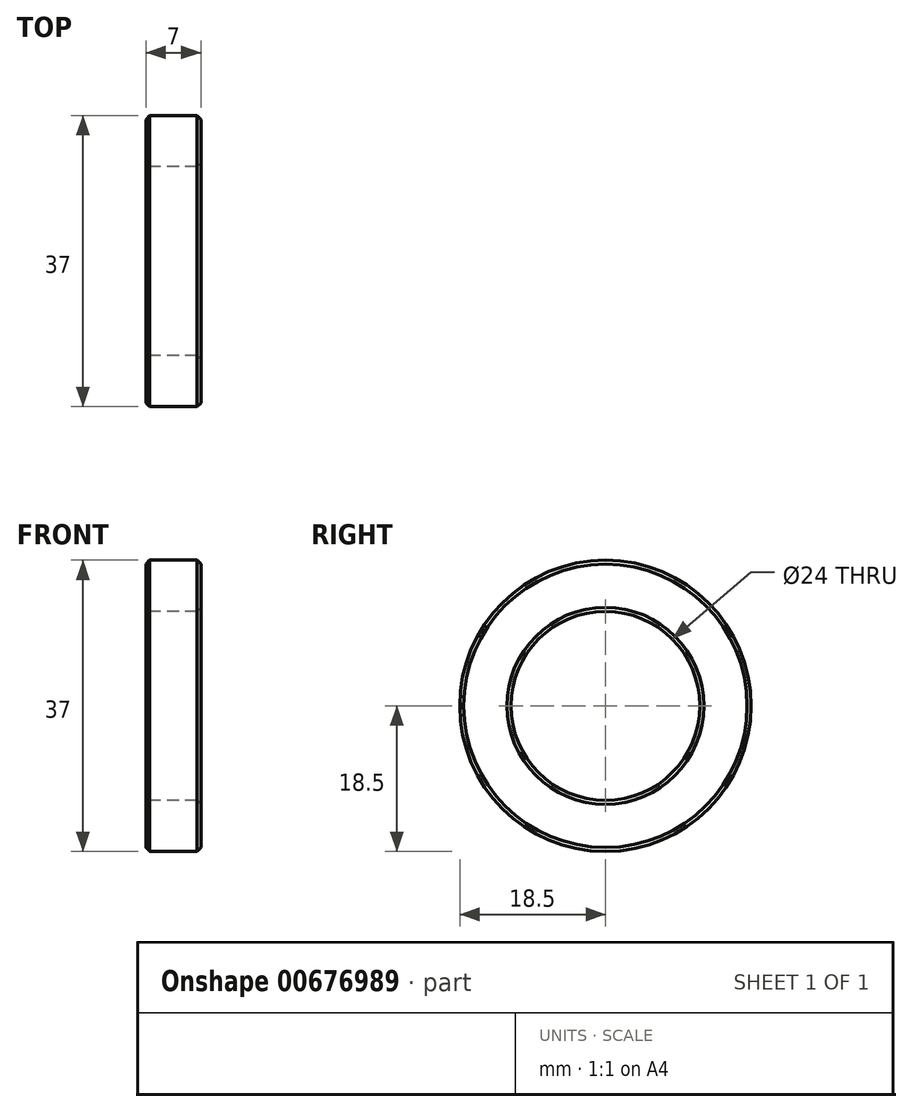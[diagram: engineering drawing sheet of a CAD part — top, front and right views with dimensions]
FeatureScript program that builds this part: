
annotation { "Feature Type Name" : "Feature", "Feature Type Description" : "" }
export const myFeature = defineFeature(function(context is Context, id is Id, definition is map)
    precondition{}
    {
        {
            var Q0;
            Q0=qCreatedBy(makeId("Right.planeOp"),FACE);
            var sketch = newSketch(context, id + "F0", { "sketchPlane" : qUnion([Q0])});
            skCircle(sketch, "E0", {"center": v(0, 0) * mm, "radius": 18.5 * mm});
            skCircle(sketch, "E1", {"center": v(0, 0) * mm, "radius": 12 * mm});
            skSolve(sketch);
        }
        {
            var Q0;
            Q0=makeQuery(id+"F0.imprint","IMPRINT",FACE,{"disambiguationData":[TD([[makeQuery(id+"F0.imprint","IMPRINT",EDGE,{"derivedFrom":sQuery(id+"F0.wireOp",EDGE,"E0")}),1.0]])]});
            extrude(context, id + "F1", {"entities" : qUnion([Q0]), "depth" : 7 * mm, "offsetDistance" : 25 * mm});
        }
        {
            var Q0;
            Q0=makeQuery(id+"F1.opExtrude","CAP_EDGE",EDGE,{"disambiguationData":[OSD([sQuery(id+"F0.wireOp",EDGE,"E0")])],"isStart":true});
            var Q1;
            Q1=makeQuery(id+"F1.opExtrude","CAP_EDGE",EDGE,{"disambiguationData":[OSD([sQuery(id+"F0.wireOp",EDGE,"E0")])],"isStart":false});
            var Q2;
            Q2=makeQuery(id+"F1.opExtrude","CAP_EDGE",EDGE,{"disambiguationData":[OSD([sQuery(id+"F0.wireOp",EDGE,"E1")])],"isStart":true});
            var Q3;
            Q3=makeQuery(id+"F1.opExtrude","CAP_EDGE",EDGE,{"disambiguationData":[OSD([sQuery(id+"F0.wireOp",EDGE,"E1")])],"isStart":false});
            chamfer(context, id + "F2", {"entities" : qUnion([Q0, Q1, Q2, Q3]), "width" : .5 * mm, "tangentPropagation" : true});
        }
    });
